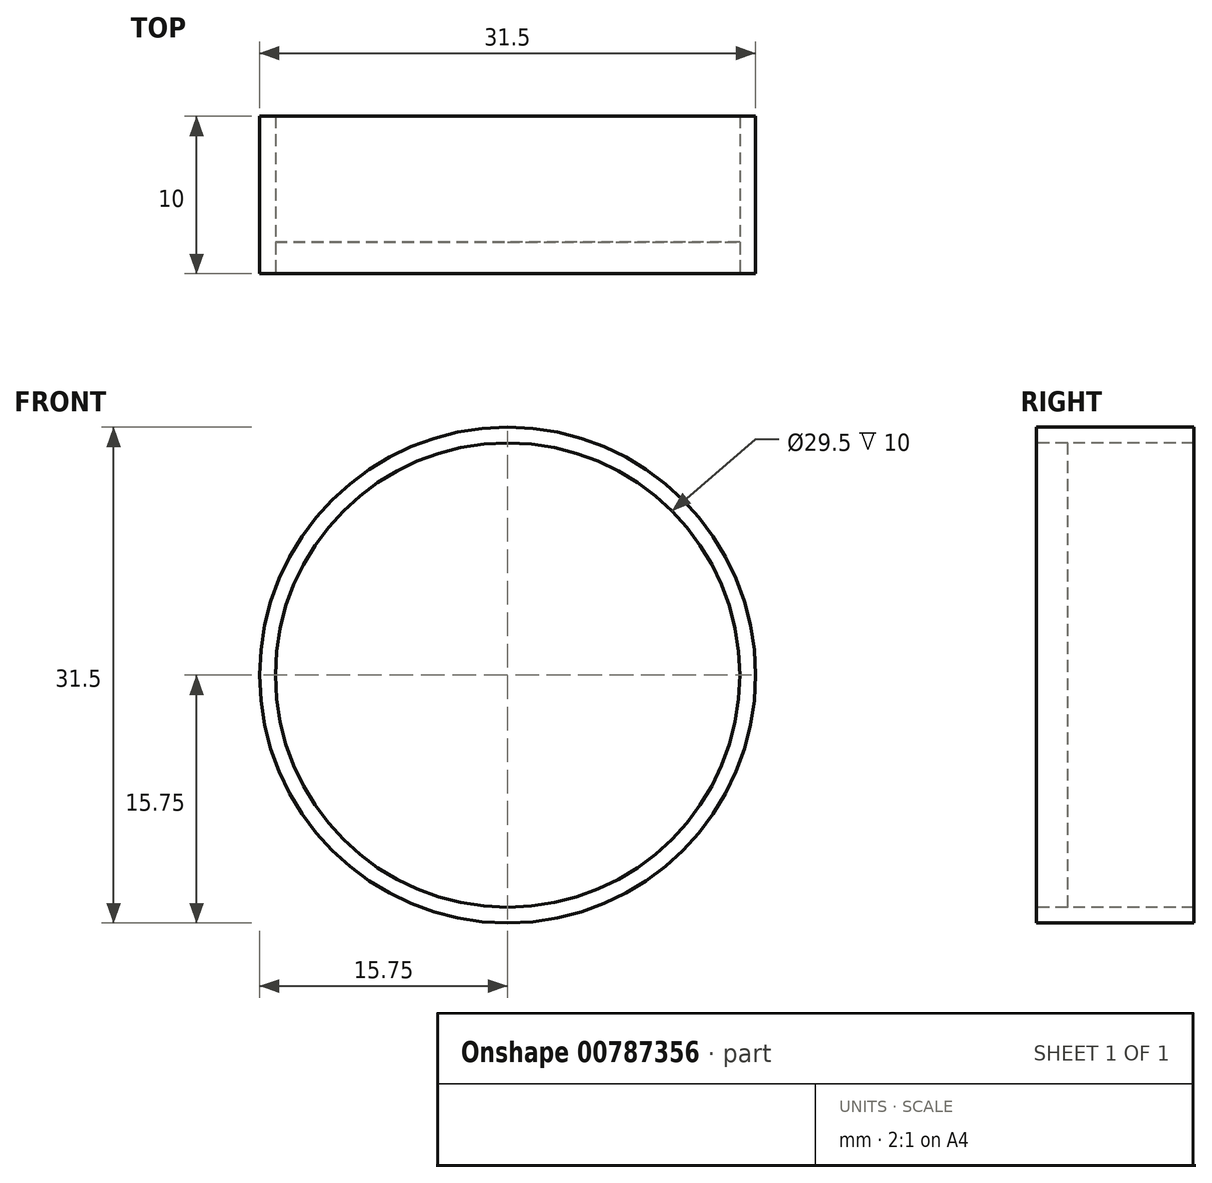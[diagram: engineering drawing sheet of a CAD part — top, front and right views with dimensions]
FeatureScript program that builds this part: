
annotation { "Feature Type Name" : "Feature", "Feature Type Description" : "" }
export const myFeature = defineFeature(function(context is Context, id is Id, definition is map)
    precondition{}
    {
        {
            var Q0;
            Q0=qCreatedBy(makeId("Front.planeOp"),FACE);
            var sketch = newSketch(context, id + "F0", { "sketchPlane" : qUnion([Q0])});
            skCircle(sketch, "E0", {"center": v(0, 0) * mm, "radius": 14.75 * mm});
            skCircle(sketch, "E1", {"center": v(0, 0) * mm, "radius": 15.75 * mm});
            skSolve(sketch);
        }
        {
            var Q0;
            Q0=makeQuery(id+"F0.imprint","IMPRINT",FACE,{"disambiguationData":[TD([[makeQuery(id+"F0.imprint","IMPRINT",EDGE,{"derivedFrom":sQuery(id+"F0.wireOp",EDGE,"E1")}),1.0]])]});
            extrude(context, id + "F1", {"entities" : qUnion([Q0]), "oppositeDirection" : true, "depth" : 10 * mm, "offsetDistance" : 25 * mm});
        }
        {
            var Q0;
            Q0=qCreatedBy(makeId("Front.planeOp"),FACE);
            var sketch = newSketch(context, id + "F2", { "sketchPlane" : qUnion([Q0])});
            skCircle(sketch, "E2", {"center": v(0, 0) * mm, "radius": 14.75 * mm});
            skSolve(sketch);
        }
        {
            var Q0;
            Q0 = qSketchRegion(id + "F2", true);
            extrude(context, id + "F3", {"entities" : qUnion([Q0]), "operationType" : NewBodyOperationType.REMOVE, "depth" : 8 * mm, "offsetDistance" : 25 * mm});
        }
        {
            var Q0;
            Q0 = qSketchRegion(id + "F2", true);
            extrude(context, id + "F4", {"entities" : qUnion([Q0]), "oppositeDirection" : true, "depth" : 2 * mm, "offsetDistance" : 25 * mm});
        }
    });
